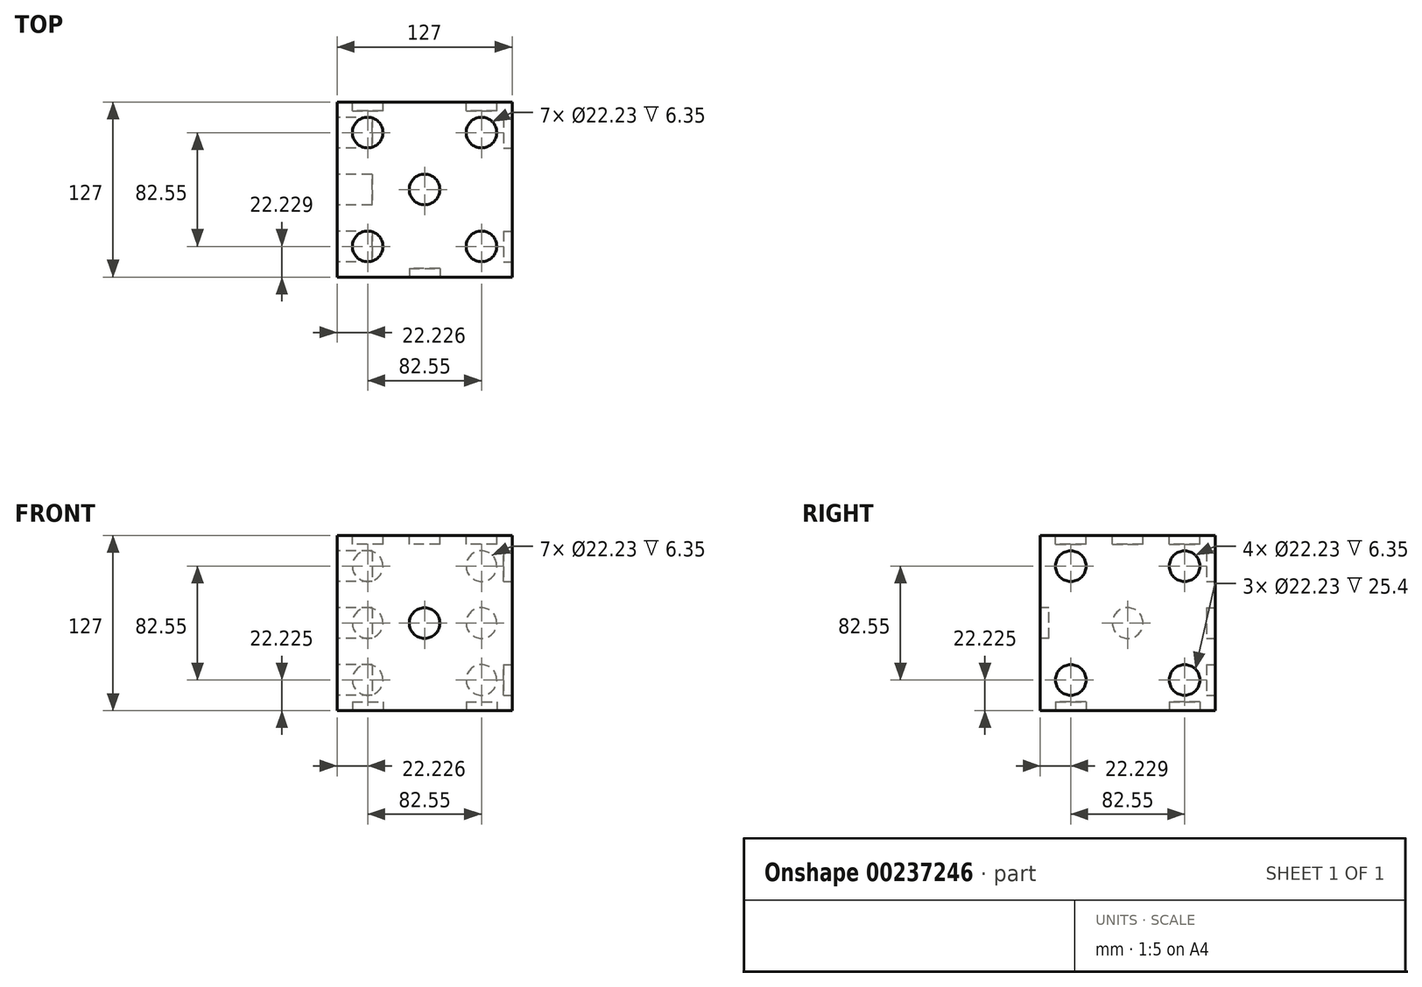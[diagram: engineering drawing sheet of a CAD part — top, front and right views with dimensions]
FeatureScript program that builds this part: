
annotation { "Feature Type Name" : "Feature", "Feature Type Description" : "" }
export const myFeature = defineFeature(function(context is Context, id is Id, definition is map)
    precondition{}
    {
        {
            var Q0;
            Q0=qCreatedBy(makeId("Top.planeOp"),FACE);
            var sketch = newSketch(context, id + "F0", { "sketchPlane" : qUnion([Q0])});
            skLineSegment(sketch, "E0.bottom", {"start": v(-87.87, -51.62) * mm, "end": v(39.13, -51.62) * mm});
            skLineSegment(sketch, "E0.top", {"start": v(-87.87, 75.38) * mm, "end": v(39.13, 75.38) * mm});
            skLineSegment(sketch, "E0.left", {"start": v(-87.87, -51.62) * mm, "end": v(-87.87, 75.38) * mm});
            skLineSegment(sketch, "E0.right", {"start": v(39.13, -51.62) * mm, "end": v(39.13, 75.38) * mm});
            skSolve(sketch);
        }
        {
            var Q0;
            Q0=makeQuery(id+"F0.imprint","IMPRINT",FACE,{"disambiguationData":[TD([[makeQuery(id+"F0.imprint","IMPRINT",EDGE,{"derivedFrom":sQuery(id+"F0.wireOp",EDGE,"E0.bottom")}),1.0]])]});
            extrude(context, id + "F1", {"entities" : qUnion([Q0]), "depth" : 127 * mm});
        }
        {
            var Q0;
            Q0=makeQuery(id+"F1.opExtrude","SWEPT_FACE",FACE,{"disambiguationData":[OSD([sQuery(id+"F0.wireOp",EDGE,"E0.bottom")])]});
            var sketch = newSketch(context, id + "F2", { "sketchPlane" : qUnion([Q0])});
            skCircle(sketch, "E1", {"center": v(-24.37, 63.5) * mm, "radius": 11.11 * mm});
            skSolve(sketch);
        }
        {
            var Q0;
            Q0=makeQuery(id+"F2.imprint","IMPRINT",FACE,{"disambiguationData":[TD([[makeQuery(id+"F2.imprint","IMPRINT",EDGE,{"derivedFrom":sQuery(id+"F2.wireOp",EDGE,"E1")}),1.0]])]});
            extrude(context, id + "F3", {"entities" : qUnion([Q0]), "operationType" : NewBodyOperationType.REMOVE, "oppositeDirection" : true, "depth" : 6.35 * mm});
        }
        {
            var Q0;
            Q0=makeQuery(id+"F1.opExtrude","SWEPT_FACE",FACE,{"disambiguationData":[OSD([sQuery(id+"F0.wireOp",EDGE,"E0.left")])]});
            var sketch = newSketch(context, id + "F4", { "sketchPlane" : qUnion([Q0])});
            skCircle(sketch, "E2", {"center": v(-11.88, 63.5) * mm, "radius": 11.11 * mm});
            skLineSegment(sketch, "E3", {"start": v(51.62, 127) * mm, "end": v(-75.38, 0) * mm, "construction": true});
            skCircle(sketch, "E4", {"center": v(29.4, 104.78) * mm, "radius": 11.11 * mm});
            skCircle(sketch, "E5", {"center": v(-53.16, 22.23) * mm, "radius": 11.11 * mm});
            skSolve(sketch);
        }
        {
            var Q0;
            Q0=makeQuery(id+"F1.opExtrude","CAP_FACE",FACE,{"disambiguationData":[OSD([sQuery(id+"F0.wireOp",EDGE,"E0.bottom"),sQuery(id+"F0.wireOp",EDGE,"E0.top"),sQuery(id+"F0.wireOp",EDGE,"E0.left"),sQuery(id+"F0.wireOp",EDGE,"E0.right")])],"isStart":false});
            var sketch = newSketch(context, id + "F5", { "sketchPlane" : qUnion([Q0])});
            skLineSegment(sketch, "E6", {"start": v(39.13, 75.38) * mm, "end": v(-87.87, -51.62) * mm, "construction": true});
            skLineSegment(sketch, "E7", {"start": v(39.13, -51.62) * mm, "end": v(-87.87, 75.38) * mm, "construction": true});
            skCircle(sketch, "E8", {"center": v(-24.37, 11.88) * mm, "radius": 11.11 * mm});
            skCircle(sketch, "E9", {"center": v(16.9, -29.4) * mm, "radius": 11.11 * mm});
            skCircle(sketch, "E10", {"center": v(16.9, 53.16) * mm, "radius": 11.11 * mm});
            skCircle(sketch, "E11", {"center": v(-65.64, 53.16) * mm, "radius": 11.11 * mm});
            skCircle(sketch, "E12", {"center": v(-65.64, -29.4) * mm, "radius": 11.11 * mm});
            skSolve(sketch);
        }
        {
            var Q0;
            Q0=makeQuery(id+"F4.imprint","IMPRINT",FACE,{"disambiguationData":[TD([[makeQuery(id+"F4.imprint","IMPRINT",EDGE,{"derivedFrom":sQuery(id+"F4.wireOp",EDGE,"E4")}),1.0]])]});
            extrude(context, id + "F6", {"entities" : qUnion([Q0]), "operationType" : NewBodyOperationType.REMOVE, "oppositeDirection" : true, "depth" : 6.35 * mm});
        }
        {
            var Q0;
            Q0 = qSketchRegion(id + "F4", true);
            extrude(context, id + "F7", {"entities" : qUnion([Q0]), "operationType" : NewBodyOperationType.REMOVE, "oppositeDirection" : true, "depth" : 25.4 * mm});
        }
        {
            var Q0;
            Q0=makeQuery(id+"F5.imprint","IMPRINT",FACE,{"disambiguationData":[TD([[makeQuery(id+"F5.imprint","IMPRINT",EDGE,{"derivedFrom":sQuery(id+"F5.wireOp",EDGE,"E9")}),1.0]])]});
            var Q1;
            Q1=makeQuery(id+"F5.imprint","IMPRINT",FACE,{"disambiguationData":[TD([[makeQuery(id+"F5.imprint","IMPRINT",EDGE,{"derivedFrom":sQuery(id+"F5.wireOp",EDGE,"E10")}),1.0]])]});
            var Q2;
            Q2=makeQuery(id+"F5.imprint","IMPRINT",FACE,{"disambiguationData":[TD([[makeQuery(id+"F5.imprint","IMPRINT",EDGE,{"derivedFrom":sQuery(id+"F5.wireOp",EDGE,"E11")}),1.0]])]});
            var Q3;
            Q3=makeQuery(id+"F5.imprint","IMPRINT",FACE,{"disambiguationData":[TD([[makeQuery(id+"F5.imprint","IMPRINT",EDGE,{"derivedFrom":sQuery(id+"F5.wireOp",EDGE,"E12")}),1.0]])]});
            extrude(context, id + "F8", {"entities" : qUnion([Q0, Q1, Q2, Q3]), "operationType" : NewBodyOperationType.REMOVE, "oppositeDirection" : true, "depth" : 6.35 * mm});
        }
        {
            var Q0;
            Q0=makeQuery(id+"F5.imprint","IMPRINT",FACE,{"disambiguationData":[TD([[makeQuery(id+"F5.imprint","IMPRINT",EDGE,{"derivedFrom":sQuery(id+"F5.wireOp",EDGE,"E8")}),1.0]])]});
            extrude(context, id + "F9", {"entities" : qUnion([Q0]), "operationType" : NewBodyOperationType.REMOVE, "oppositeDirection" : true, "depth" : 6.35 * mm});
        }
        {
            var Q0;
            Q0=makeQuery(id+"F1.opExtrude","SWEPT_FACE",FACE,{"disambiguationData":[OSD([sQuery(id+"F0.wireOp",EDGE,"E0.top")])]});
            var sketch = newSketch(context, id + "F10", { "sketchPlane" : qUnion([Q0])});
            skLineSegment(sketch, "E13", {"start": v(-16.9, 127) * mm, "end": v(-16.9, 0) * mm, "construction": true});
            skCircle(sketch, "E14", {"center": v(-16.9, 104.78) * mm, "radius": 11.11 * mm});
            skCircle(sketch, "E15", {"center": v(-16.9, 63.5) * mm, "radius": 11.11 * mm});
            skCircle(sketch, "E16", {"center": v(-16.9, 22.23) * mm, "radius": 11.11 * mm});
            skLineSegment(sketch, "E17", {"start": v(65.64, 127) * mm, "end": v(65.64, 0) * mm, "construction": true});
            skCircle(sketch, "E18", {"center": v(65.64, 104.78) * mm, "radius": 11.11 * mm});
            skCircle(sketch, "E19", {"center": v(65.64, 63.5) * mm, "radius": 11.11 * mm});
            skCircle(sketch, "E20", {"center": v(65.64, 22.23) * mm, "radius": 11.11 * mm});
            skSolve(sketch);
        }
        {
            var Q0;
            Q0=makeQuery(id+"F10.imprint","IMPRINT",FACE,{"disambiguationData":[TD([[makeQuery(id+"F10.imprint","IMPRINT",EDGE,{"derivedFrom":sQuery(id+"F10.wireOp",EDGE,"E14")}),1.0]])]});
            var Q1;
            Q1=makeQuery(id+"F10.imprint","IMPRINT",FACE,{"disambiguationData":[TD([[makeQuery(id+"F10.imprint","IMPRINT",EDGE,{"derivedFrom":sQuery(id+"F10.wireOp",EDGE,"E15")}),1.0]])]});
            var Q2;
            Q2=makeQuery(id+"F10.imprint","IMPRINT",FACE,{"disambiguationData":[TD([[makeQuery(id+"F10.imprint","IMPRINT",EDGE,{"derivedFrom":sQuery(id+"F10.wireOp",EDGE,"E16")}),1.0]])]});
            var Q3;
            Q3=makeQuery(id+"F10.imprint","IMPRINT",FACE,{"disambiguationData":[TD([[makeQuery(id+"F10.imprint","IMPRINT",EDGE,{"derivedFrom":sQuery(id+"F10.wireOp",EDGE,"E20")}),1.0]])]});
            var Q4;
            Q4=makeQuery(id+"F10.imprint","IMPRINT",FACE,{"disambiguationData":[TD([[makeQuery(id+"F10.imprint","IMPRINT",EDGE,{"derivedFrom":sQuery(id+"F10.wireOp",EDGE,"E19")}),1.0]])]});
            var Q5;
            Q5=makeQuery(id+"F10.imprint","IMPRINT",FACE,{"disambiguationData":[TD([[makeQuery(id+"F10.imprint","IMPRINT",EDGE,{"derivedFrom":sQuery(id+"F10.wireOp",EDGE,"E18")}),1.0]])]});
            extrude(context, id + "F11", {"entities" : qUnion([Q0, Q1, Q2, Q3, Q4, Q5]), "operationType" : NewBodyOperationType.REMOVE, "oppositeDirection" : true, "depth" : 6.35 * mm});
        }
        {
            var Q0;
            Q0=makeQuery(id+"F1.opExtrude","CAP_FACE",FACE,{"disambiguationData":[OSD([sQuery(id+"F0.wireOp",EDGE,"E0.bottom"),sQuery(id+"F0.wireOp",EDGE,"E0.top"),sQuery(id+"F0.wireOp",EDGE,"E0.left"),sQuery(id+"F0.wireOp",EDGE,"E0.right")])],"isStart":true});
            var sketch = newSketch(context, id + "F12", { "sketchPlane" : qUnion([Q0])});
            skLineSegment(sketch, "E21", {"start": v(-87.87, -75.38) * mm, "end": v(39.13, 51.62) * mm, "construction": true});
            skCircle(sketch, "E22", {"center": v(16.9, 29.4) * mm, "radius": 11.11 * mm});
            skCircle(sketch, "E23", {"center": v(-65.64, -53.16) * mm, "radius": 11.11 * mm});
            skSolve(sketch);
        }
        {
            var Q0;
            Q0=makeQuery(id+"F1.opExtrude","SWEPT_FACE",FACE,{"disambiguationData":[OSD([sQuery(id+"F0.wireOp",EDGE,"E0.right")])]});
            var sketch = newSketch(context, id + "F13", { "sketchPlane" : qUnion([Q0])});
            skLineSegment(sketch, "E24", {"start": v(-51.62, 22.22) * mm, "end": v(75.38, 22.23) * mm, "construction": true});
            skLineSegment(sketch, "E25", {"start": v(-51.62, 104.77) * mm, "end": v(75.38, 104.78) * mm, "construction": true});
            skLineSegment(sketch, "E26", {"start": v(53.16, 0) * mm, "end": v(53.16, 127) * mm, "construction": true});
            skLineSegment(sketch, "E27", {"start": v(-29.4, 0) * mm, "end": v(-29.4, 127) * mm, "construction": true});
            skCircle(sketch, "E28", {"center": v(-29.4, 22.22) * mm, "radius": 11.11 * mm});
            skCircle(sketch, "E29", {"center": v(-29.4, 104.77) * mm, "radius": 11.11 * mm});
            skCircle(sketch, "E30", {"center": v(53.16, 104.78) * mm, "radius": 11.11 * mm});
            skCircle(sketch, "E31", {"center": v(53.16, 22.23) * mm, "radius": 11.11 * mm});
            skSolve(sketch);
        }
        {
            var Q0;
            Q0=makeQuery(id+"F13.imprint","IMPRINT",FACE,{"disambiguationData":[TD([[makeQuery(id+"F13.imprint","IMPRINT",EDGE,{"derivedFrom":sQuery(id+"F13.wireOp",EDGE,"E30")}),1.0]])]});
            var Q1;
            Q1=makeQuery(id+"F13.imprint","IMPRINT",FACE,{"disambiguationData":[TD([[makeQuery(id+"F13.imprint","IMPRINT",EDGE,{"derivedFrom":sQuery(id+"F13.wireOp",EDGE,"E31")}),1.0]])]});
            var Q2;
            Q2=makeQuery(id+"F13.imprint","IMPRINT",FACE,{"disambiguationData":[TD([[makeQuery(id+"F13.imprint","IMPRINT",EDGE,{"derivedFrom":sQuery(id+"F13.wireOp",EDGE,"E28")}),1.0]])]});
            var Q3;
            Q3=makeQuery(id+"F13.imprint","IMPRINT",FACE,{"disambiguationData":[TD([[makeQuery(id+"F13.imprint","IMPRINT",EDGE,{"derivedFrom":sQuery(id+"F13.wireOp",EDGE,"E29")}),1.0]])]});
            extrude(context, id + "F14", {"entities" : qUnion([Q0, Q1, Q2, Q3]), "operationType" : NewBodyOperationType.REMOVE, "oppositeDirection" : true, "depth" : 6.35 * mm});
        }
        {
            var Q0;
            Q0=makeQuery(id+"F12.imprint","IMPRINT",FACE,{"disambiguationData":[TD([[makeQuery(id+"F12.imprint","IMPRINT",EDGE,{"derivedFrom":sQuery(id+"F12.wireOp",EDGE,"E23")}),1.0]])]});
            var Q1;
            Q1=makeQuery(id+"F12.imprint","IMPRINT",FACE,{"disambiguationData":[TD([[makeQuery(id+"F12.imprint","IMPRINT",EDGE,{"derivedFrom":sQuery(id+"F12.wireOp",EDGE,"E22")}),1.0]])]});
            extrude(context, id + "F15", {"entities" : qUnion([Q0, Q1]), "operationType" : NewBodyOperationType.REMOVE, "oppositeDirection" : true, "depth" : 6.35 * mm});
        }
    });
